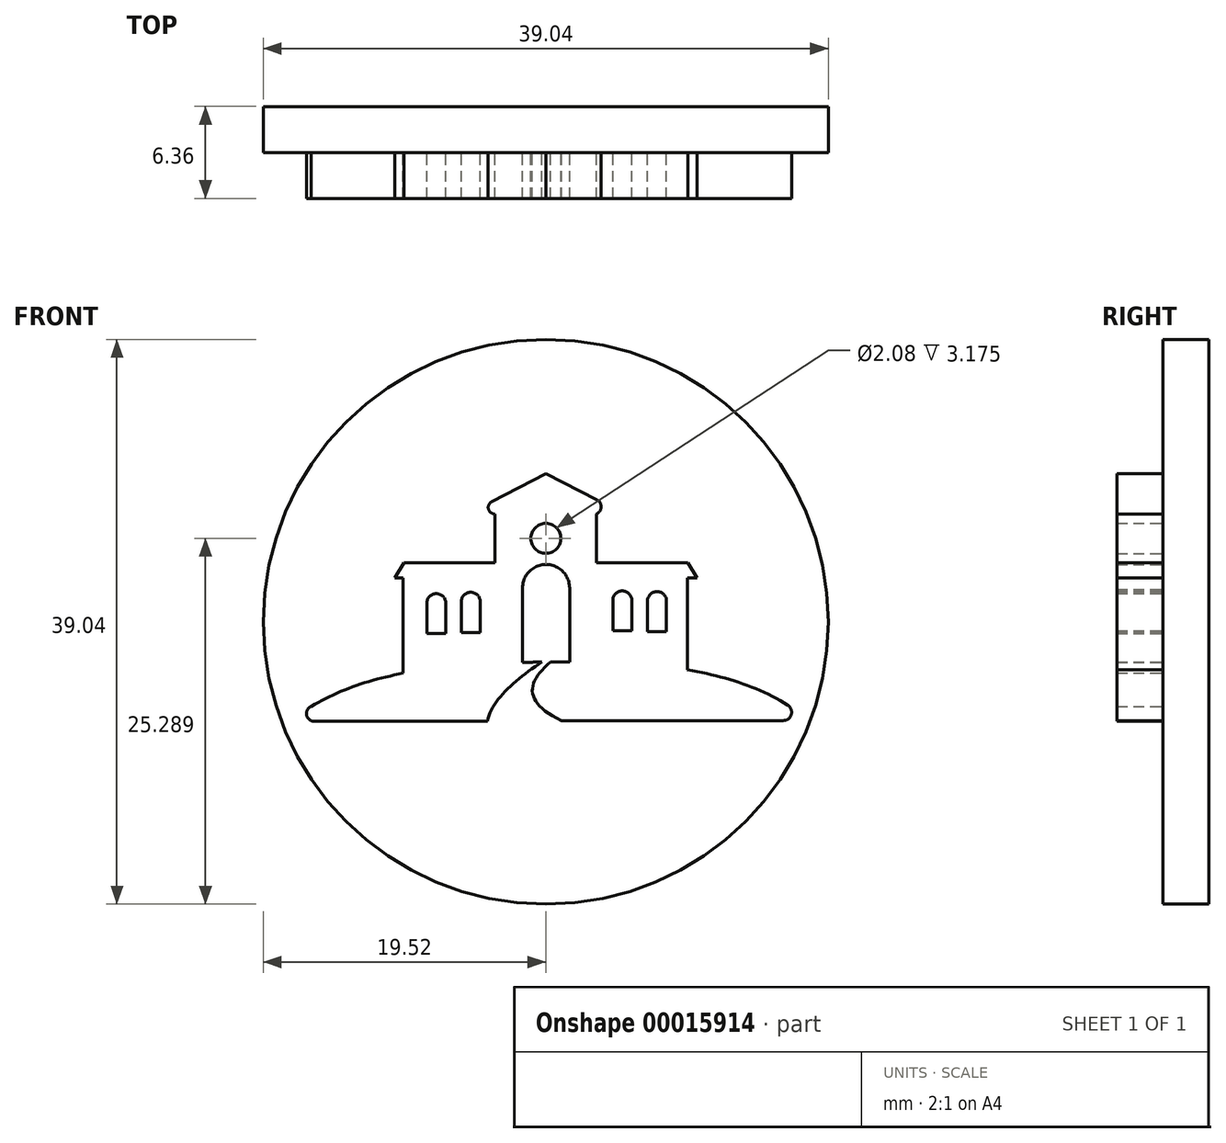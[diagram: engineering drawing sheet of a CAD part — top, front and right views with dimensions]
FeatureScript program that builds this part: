
annotation { "Feature Type Name" : "Feature", "Feature Type Description" : "" }
export const myFeature = defineFeature(function(context is Context, id is Id, definition is map)
    precondition{}
    {
        {
            var Q0;
            Q0=qCreatedBy(makeId("Front.planeOp"),FACE);
            var sketch = newSketch(context, id + "F0", { "sketchPlane" : qUnion([Q0])});
            skLineSegment(sketch, "E0.bottom", {"start": v(-3.53, 5.08) * mm, "end": v(3.5, 5.08) * mm});
            skLineSegment(sketch, "E0.top", {"start": v(-3.53, 15.32) * mm, "end": v(3.5, 15.32) * mm});
            skLineSegment(sketch, "E0.left", {"start": v(-3.53, 5.08) * mm, "end": v(-3.53, 15.32) * mm});
            skLineSegment(sketch, "E0.right", {"start": v(3.5, 5.08) * mm, "end": v(3.5, 15.32) * mm});
            skLineSegment(sketch, "E1.bottom", {"start": v(-9.86, 10.9) * mm, "end": v(-3.53, 10.9) * mm});
            skLineSegment(sketch, "E1.top", {"start": v(-9.86, 5.08) * mm, "end": v(-3.53, 5.08) * mm});
            skLineSegment(sketch, "E1.left", {"start": v(-9.86, 10.9) * mm, "end": v(-9.86, 5.08) * mm});
            skLineSegment(sketch, "E1.right", {"start": v(-3.53, 10.9) * mm, "end": v(-3.53, 5.08) * mm});
            skLineSegment(sketch, "E2.bottom", {"start": v(9.8, 10.9) * mm, "end": v(3.5, 10.9) * mm});
            skLineSegment(sketch, "E2.top", {"start": v(9.8, 5.08) * mm, "end": v(3.5, 5.08) * mm});
            skLineSegment(sketch, "E2.left", {"start": v(9.8, 10.9) * mm, "end": v(9.8, 5.08) * mm});
            skLineSegment(sketch, "E2.right", {"start": v(3.5, 10.9) * mm, "end": v(3.5, 5.08) * mm});
            skCircle(sketch, "E3", {"center": v(0, 13.63) * mm, "radius": 1.04 * mm});
            skPoint(sketch, "E3.centerSnap0", {"position": v(0, 15.11) * mm});
            skLineSegment(sketch, "E4", {"start": v(-1.6, 10.1) * mm, "end": v(-1.6, 5.08) * mm});
            skLineSegment(sketch, "E5", {"start": v(-1.6, 5.08) * mm, "end": v(1.64, 5.08) * mm});
            skLineSegment(sketch, "E6", {"start": v(1.64, 5.08) * mm, "end": v(1.64, 10.2) * mm});
            skPoint(sketch, "E6.endSnap0", {"position": v(3.5, 10.2) * mm});
            skLineSegment(sketch, "E7", {"start": v(0, 40.22) * mm, "end": v(0, 0) * mm, "construction": true});
            skArc(sketch, "E8", {"start": v(1.64, 10.2) * mm, "mid": v(-0.03, 11.82) * mm, "end": v(-1.6, 10.1) * mm});
            skLineSegment(sketch, "E9", {"start": v(0, 18.1) * mm, "end": v(-3.74, 16.16) * mm});
            skLineSegment(sketch, "E10", {"start": v(3.53, 16.3) * mm, "end": v(0, 18.1) * mm});
            skArc(sketch, "E11", {"start": v(3.53, 16.3) * mm, "mid": v(3.83, 15.8) * mm, "end": v(3.5, 15.32) * mm});
            skLineSegment(sketch, "E12", {"start": v(3.5, 11.96) * mm, "end": v(9.81, 11.96) * mm});
            skLineSegment(sketch, "E13", {"start": v(9.81, 11.96) * mm, "end": v(10.47, 10.9) * mm});
            skLineSegment(sketch, "E14", {"start": v(-3.53, 11.96) * mm, "end": v(-9.8, 11.96) * mm});
            skLineSegment(sketch, "E15", {"start": v(-9.8, 11.96) * mm, "end": v(-10.45, 10.9) * mm});
            skLineSegment(sketch, "E16", {"start": v(-10.45, 10.9) * mm, "end": v(-9.86, 10.9) * mm});
            skLineSegment(sketch, "E17", {"start": v(9.8, 10.9) * mm, "end": v(10.47, 10.9) * mm});
            skPoint(sketch, "E18.1.internal.snap0", {"position": v(0.02, 5.08) * mm});
            skFitSpline(sketch, "E18", {"points": [v(-16.21, 2) * mm, v(0, 5.08) * mm, v(16.72, 2.1) * mm], "startDerivative": vector(25.49, 15.73) * mm, "endDerivative": vector(26.19, -16.57) * mm});
            skLineSegment(sketch, "E19", {"start": v(-16.02, 0.98) * mm, "end": v(-4.04, 0.98) * mm});
            skLineSegment(sketch, "E20", {"start": v(1.07, 1.04) * mm, "end": v(16.41, 1.04) * mm});
            skArc(sketch, "E21", {"start": v(-16.02, 0.98) * mm, "mid": v(-16.54, 1.41) * mm, "end": v(-16.21, 2) * mm});
            skArc(sketch, "E22", {"start": v(16.41, 1.04) * mm, "mid": v(16.96, 1.45) * mm, "end": v(16.72, 2.1) * mm});
            skLineSegment(sketch, "E23", {"start": v(-8.23, 9.15) * mm, "end": v(-8.23, 7.04) * mm});
            skLineSegment(sketch, "E24", {"start": v(-8.23, 7.04) * mm, "end": v(-6.91, 7.04) * mm});
            skLineSegment(sketch, "E25", {"start": v(-6.91, 7.04) * mm, "end": v(-6.91, 9.15) * mm});
            skLineSegment(sketch, "E26", {"start": v(-6.91, 9.15) * mm, "end": v(-8.23, 9.15) * mm, "construction": true});
            skArc(sketch, "E27", {"start": v(-6.91, 9.15) * mm, "mid": v(-7.57, 9.8) * mm, "end": v(-8.23, 9.15) * mm});
            skLineSegment(sketch, "E28", {"start": v(-4.53, 7.13) * mm, "end": v(-4.53, 9.24) * mm});
            skArc(sketch, "E29", {"start": v(-4.53, 9.24) * mm, "mid": v(-5.19, 9.9) * mm, "end": v(-5.85, 9.24) * mm});
            skLineSegment(sketch, "E30", {"start": v(-5.85, 9.24) * mm, "end": v(-5.85, 7.13) * mm});
            skLineSegment(sketch, "E31", {"start": v(-5.85, 7.13) * mm, "end": v(-4.53, 7.13) * mm});
            skLineSegment(sketch, "E32", {"start": v(5.94, 7.23) * mm, "end": v(5.94, 9.35) * mm});
            skArc(sketch, "E33", {"start": v(5.94, 9.35) * mm, "mid": v(5.28, 10) * mm, "end": v(4.63, 9.35) * mm});
            skLineSegment(sketch, "E34", {"start": v(4.63, 9.35) * mm, "end": v(4.63, 7.23) * mm});
            skLineSegment(sketch, "E35", {"start": v(4.63, 7.23) * mm, "end": v(5.94, 7.23) * mm});
            skLineSegment(sketch, "E36", {"start": v(8.34, 7.18) * mm, "end": v(8.34, 9.3) * mm});
            skArc(sketch, "E37", {"start": v(8.34, 9.3) * mm, "mid": v(7.68, 9.95) * mm, "end": v(7.02, 9.3) * mm});
            skLineSegment(sketch, "E38", {"start": v(7.02, 9.3) * mm, "end": v(7.02, 7.18) * mm});
            skLineSegment(sketch, "E39", {"start": v(7.02, 7.18) * mm, "end": v(8.34, 7.18) * mm});
            skArc(sketch, "E40", {"start": v(-3.74, 16.16) * mm, "mid": v(-3.97, 15.66) * mm, "end": v(-3.53, 15.32) * mm});
            skFitSpline(sketch, "E41", {"points": [v(-0.26, 5.08) * mm, v(-4.04, 0.98) * mm], "startDerivative": vector(-5.42, -3.55) * mm, "endDerivative": vector(-0.87, -4.44) * mm});
            skFitSpline(sketch, "E42", {"points": [v(0.34, 5.08) * mm, v(1.07, 1.04) * mm], "startDerivative": vector(-5.2, -4.32) * mm, "endDerivative": vector(7.82, -3.78) * mm});
            skSolve(sketch);
        }
        {
            var Q0;
            Q0=qCreatedBy(makeId("Front.planeOp"),FACE);
            var sketch = newSketch(context, id + "F1", { "sketchPlane" : qUnion([Q0])});
            skCircle(sketch, "E43", {"center": v(0, 7.86) * mm, "radius": 19.52 * mm});
            skSolve(sketch);
        }
        {
            var Q0;
            Q0 = qSketchRegion(id + "F1", true);
            extrude(context, id + "F2", {"entities" : qUnion([Q0]), "oppositeDirection" : true, "depth" : 3.17 * mm});
        }
        {
            var Q0;
            Q0=makeQuery(id+"F0.imprint","IMPRINT",FACE,{"disambiguationData":[TD([[makeQuery(id+"F0.imprint","IMPRINT",EDGE,{"derivedFrom":sQuery(id+"F0.wireOp",EDGE,"E19")}),1.0]])]});
            var Q1;
            Q1=makeQuery(id+"F0.imprint","IMPRINT",FACE,{"disambiguationData":[TD([[makeQuery(id+"F0.imprint","IMPRINT",EDGE,{"derivedFrom":sQuery(id+"F0.wireOp",EDGE,"E1.bottom")}),-1.0]])]});
            var Q2;
            {var subQ1=sQuery(id+"F0.wireOp",EDGE,"E1.bottom");Q2=makeQuery(id+"F0.imprint","IMPRINT",FACE,{"disambiguationData":[TD([[makeQuery(id+"F0.imprint","IMPRINT",EDGE,{"derivedFrom":subQ1}),1.0]])]});}
            var Q3;
            {var subQ2=sQuery(id+"F0.wireOp",EDGE,"E0.top");Q3=makeQuery(id+"F0.imprint","IMPRINT",FACE,{"disambiguationData":[TD([[makeQuery(id+"F0.imprint","IMPRINT",EDGE,{"derivedFrom":subQ2}),-1.0]])]});}
            var Q4;
            Q4=makeQuery(id+"F0.imprint","IMPRINT",FACE,{"disambiguationData":[TD([[makeQuery(id+"F0.imprint","IMPRINT",EDGE,{"derivedFrom":sQuery(id+"F0.wireOp",EDGE,"E0.top")}),1.0]])]});
            var Q5;
            {var subQ1=sQuery(id+"F0.wireOp",EDGE,"E2.bottom");Q5=makeQuery(id+"F0.imprint","IMPRINT",FACE,{"disambiguationData":[TD([[makeQuery(id+"F0.imprint","IMPRINT",EDGE,{"derivedFrom":subQ1}),-1.0]])]});}
            var Q6;
            Q6=makeQuery(id+"F0.imprint","IMPRINT",FACE,{"disambiguationData":[TD([[makeQuery(id+"F0.imprint","IMPRINT",EDGE,{"derivedFrom":sQuery(id+"F0.wireOp",EDGE,"E2.bottom")}),1.0]])]});
            var Q7;
            Q7=sQuery(id+"F0.wireOp",EDGE,"E36");
            var Q8;
            Q8=sQuery(id+"F0.wireOp",EDGE,"E37");
            var Q9;
            Q9=sQuery(id+"F0.wireOp",EDGE,"E38");
            var Q10;
            Q10=sQuery(id+"F0.wireOp",EDGE,"E39");
            extrude(context, id + "F3", {"entities" : qUnion([Q0, Q1, Q2, Q3, Q4, Q5, Q6]), "operationType" : NewBodyOperationType.ADD, "surfaceEntities" : qUnion([Q7, Q8, Q9, Q10]), "depth" : 3.17 * mm});
        }
        {
            var Q0;
            {var subQ0=sQuery(id+"F0.wireOp",EDGE,"E20");Q0=makeQuery(id+"F0.imprint","IMPRINT",FACE,{"disambiguationData":[TD([[makeQuery(id+"F0.imprint","IMPRINT",EDGE,{"derivedFrom":subQ0}),1.0]])]});}
            extrude(context, id + "F4", {"entities" : qUnion([Q0]), "depth" : 3.17 * mm});
        }
        {
            var Q0;
            {var subQ5=sQuery(id+"F1.wireOp",EDGE,"E43");Q0=makeQuery(id+"F3.boolean.opBoolean","SPLIT",FACE,{"disambiguationData":[TD([makeQuery(id+"F2.opExtrude","SWEPT_FACE",FACE,{"disambiguationData":[OSD([subQ5])]})])],"derivedFrom":makeQuery(id+"F2.opExtrude","CAP_FACE",FACE,{"disambiguationData":[OSD([subQ5])],"isStart":true})});}
            var sketch = newSketch(context, id + "F5", { "sketchPlane" : qUnion([Q0])});
            skLineSegment(sketch, "E44", {"start": v(-9.86, 5.08) * mm, "end": v(-9.86, 3.7) * mm});
            skLineSegment(sketch, "E45", {"start": v(-9.86, 3.7) * mm, "end": v(-1.6, 4.58) * mm});
            skLineSegment(sketch, "E46", {"start": v(-1.6, 4.58) * mm, "end": v(-1.6, 5.08) * mm});
            skLineSegment(sketch, "E47", {"start": v(1.64, 5.85) * mm, "end": v(1.64, 4) * mm});
            skLineSegment(sketch, "E48", {"start": v(1.64, 4) * mm, "end": v(9.8, 4) * mm});
            skLineSegment(sketch, "E49", {"start": v(9.8, 4) * mm, "end": v(9.8, 5.08) * mm});
            skLineSegment(sketch, "E50.0", {"start": v(-9.86, 5.08) * mm, "end": v(-1.6, 5.08) * mm});
            skLineSegment(sketch, "E51", {"start": v(1.64, 5.85) * mm, "end": v(9.8, 5.08) * mm});
            skSolve(sketch);
        }
        {
            var Q0;
            Q0 = qSketchRegion(id + "F5", true);
            var Q1;
            Q1=makeQuery(id+"F3.opExtrude","CAP_FACE",FACE,{"disambiguationData":[OSD([sQuery(id+"F0.wireOp",EDGE,"E0.bottom"),sQuery(id+"F0.wireOp",EDGE,"E0.left"),sQuery(id+"F0.wireOp",EDGE,"E0.right"),sQuery(id+"F0.wireOp",EDGE,"E1.top"),sQuery(id+"F0.wireOp",EDGE,"E1.left"),sQuery(id+"F0.wireOp",EDGE,"E2.top"),sQuery(id+"F0.wireOp",EDGE,"E2.left"),sQuery(id+"F0.wireOp",EDGE,"E3"),sQuery(id+"F0.wireOp",EDGE,"E4"),sQuery(id+"F0.wireOp",EDGE,"E6"),sQuery(id+"F0.wireOp",EDGE,"E8"),sQuery(id+"F0.wireOp",EDGE,"E9"),sQuery(id+"F0.wireOp",EDGE,"E10"),sQuery(id+"F0.wireOp",EDGE,"E11"),sQuery(id+"F0.wireOp",EDGE,"E12"),sQuery(id+"F0.wireOp",EDGE,"E13"),sQuery(id+"F0.wireOp",EDGE,"E14"),sQuery(id+"F0.wireOp",EDGE,"E15"),sQuery(id+"F0.wireOp",EDGE,"E16"),sQuery(id+"F0.wireOp",EDGE,"E17"),sQuery(id+"F0.wireOp",EDGE,"E18"),sQuery(id+"F0.wireOp",EDGE,"E23"),sQuery(id+"F0.wireOp",EDGE,"E24"),sQuery(id+"F0.wireOp",EDGE,"E25"),sQuery(id+"F0.wireOp",EDGE,"E27"),sQuery(id+"F0.wireOp",EDGE,"E28"),sQuery(id+"F0.wireOp",EDGE,"E29"),sQuery(id+"F0.wireOp",EDGE,"E30"),sQuery(id+"F0.wireOp",EDGE,"E31"),sQuery(id+"F0.wireOp",EDGE,"E32"),sQuery(id+"F0.wireOp",EDGE,"E33"),sQuery(id+"F0.wireOp",EDGE,"E34"),sQuery(id+"F0.wireOp",EDGE,"E35"),sQuery(id+"F0.wireOp",EDGE,"E36"),sQuery(id+"F0.wireOp",EDGE,"E37"),sQuery(id+"F0.wireOp",EDGE,"E38"),sQuery(id+"F0.wireOp",EDGE,"E39"),sQuery(id+"F0.wireOp",EDGE,"E40")])],"isStart":false});
            extrude(context, id + "F6", {"entities" : qUnion([Q0]), "operationType" : NewBodyOperationType.ADD, "endBound" : BoundingType.UP_TO_SURFACE, "endBoundEntityFace" : qUnion([Q1]), "depth" : 25.4 * mm});
        }
    });
